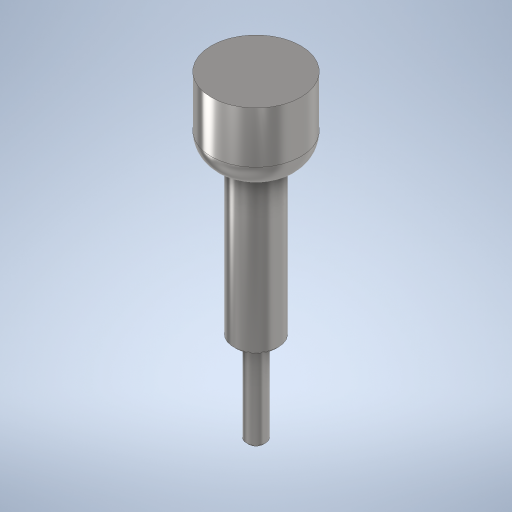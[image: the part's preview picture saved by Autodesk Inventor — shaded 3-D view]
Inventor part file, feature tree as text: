
AUTODESK INVENTOR PART (.ipt)
format: ipt  version: 2024.3 (Build 283343000, 343)  size: 260,096 bytes
history: native  units: mm
features: extrude x3, sketch x3, fillet x1, chamfer x1
ambient origin geometry x8: Origin, YZ Plane, XZ Plane, XY Plane, X Axis, Y Axis, Z Axis, Center Point
bodies: Solido1 (feature_tree)
feature tree (8):
  extrude  "Estrusione1"  Depth=0.07mm
  extrude  "Estrusione5"  Depth=0.06mm TaperAngle=0.0deg
  extrude  "Estrusione6"  Depth=0.035mm
  fillet  "Raccordo4"  Radius=0.19mm
  chamfer  "Smusso2"  Distance=0.015mm
  sketch  "Schizzo1"
  sketch  "Schizzo6"
  sketch  "Schizzo7"
